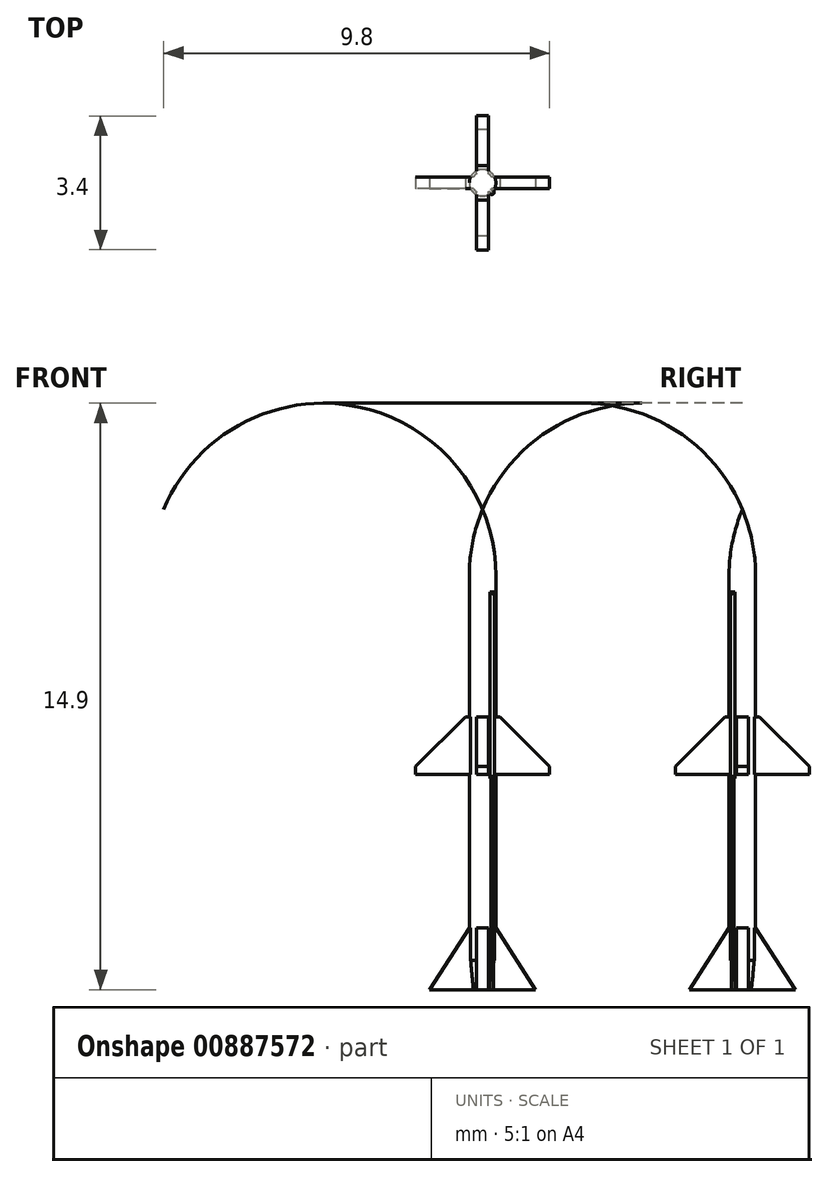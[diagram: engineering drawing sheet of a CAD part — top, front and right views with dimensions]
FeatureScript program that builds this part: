
annotation { "Feature Type Name" : "Feature", "Feature Type Description" : "" }
export const myFeature = defineFeature(function(context is Context, id is Id, definition is map)
    precondition{}
    {
        {
            var Q0;
            Q0=qCreatedBy(makeId("Front.planeOp"),FACE);
            var sketch = newSketch(context, id + "F0", { "sketchPlane" : qUnion([Q0])});
            skLineSegment(sketch, "E0", {"start": v(0, 0) * mm, "end": v(0, 12.2) * mm});
            skLineSegment(sketch, "E1", {"start": v(0.34, 10.5) * mm, "end": v(0.34, 0) * mm});
            skLineSegment(sketch, "E2", {"start": v(0.34, 0) * mm, "end": v(0, 0) * mm});
            skArc(sketch, "E3", {"start": v(0.34, 10.5) * mm, "mid": v(0.25, 11.37) * mm, "end": v(0, 12.2) * mm});
            skSolve(sketch);
        }
        {
            var Q0;
            Q0=makeQuery(id+"F0.imprint","IMPRINT",FACE,{"disambiguationData":[TD([[makeQuery(id+"F0.imprint","IMPRINT",EDGE,{"derivedFrom":sQuery(id+"F0.wireOp",EDGE,"E0")}),-1.0]])]});
            var Q1;
            Q1=sQuery(id+"F0.wireOp",EDGE,"E0");
            revolve(context, id + "F1", {"surfaceOperationType" : NewSurfaceOperationType.NEW, "entities" : qUnion([Q0]), "axis" : qUnion([Q1]), "revolveType" : RevolveType.FULL});
        }
        {
            var Q0;
            Q0=qCreatedBy(makeId("Front.planeOp"),FACE);
            var sketch = newSketch(context, id + "F2", { "sketchPlane" : qUnion([Q0])});
            skLineSegment(sketch, "E4", {"start": v(0.28, 0) * mm, "end": v(0.34, 0.75) * mm});
            skLineSegment(sketch, "E5", {"start": v(0.34, 0.75) * mm, "end": v(1.27, 0.75) * mm});
            skLineSegment(sketch, "E6", {"start": v(1.27, 0.75) * mm, "end": v(1.27, 0) * mm});
            skLineSegment(sketch, "E7", {"start": v(1.27, 0) * mm, "end": v(0.28, 0) * mm});
            skLineSegment(sketch, "E8.0", {"start": v(0.34, 0) * mm, "end": v(-0.34, 0) * mm});
            skSolve(sketch);
        }
        {
            var Q0;
            Q0=qSketchRegion(id+"F2",true);
            var Q1;
            Q1=makeQuery(id+"F1.opRevolve","SWEPT_FACE",FACE,{"disambiguationData":[OSD([sQuery(id+"F0.wireOp",EDGE,"E1")])]});
            revolve(context, id + "F3", {"operationType" : NewBodyOperationType.REMOVE, "surfaceOperationType" : NewSurfaceOperationType.NEW, "entities" : qUnion([Q0]), "axis" : qUnion([Q1]), "revolveType" : RevolveType.FULL, "oppositeDirection" : true});
        }
        {
            var Q0;
            Q0=qCreatedBy(makeId("Front.planeOp"),FACE);
            var sketch = newSketch(context, id + "F4", { "sketchPlane" : qUnion([Q0])});
            skLineSegment(sketch, "E9", {"start": v(-0.34, 6.93) * mm, "end": v(0.34, 6.93) * mm});
            skLineSegment(sketch, "E10", {"start": v(1.7, 5.47) * mm, "end": v(0.34, 5.47) * mm});
            skLineSegment(sketch, "E11", {"start": v(0.34, 1.57) * mm, "end": v(1.35, 0) * mm});
            skLineSegment(sketch, "E12", {"start": v(1.35, 0) * mm, "end": v(-1.35, 0) * mm});
            skLineSegment(sketch, "E13", {"start": v(-1.35, 0) * mm, "end": v(-0.34, 1.57) * mm});
            skLineSegment(sketch, "E14", {"start": v(-0.34, 5.47) * mm, "end": v(-1.7, 5.47) * mm});
            skLineSegment(sketch, "E15.0", {"start": v(0.34, 10.5) * mm, "end": v(-0.34, 10.5) * mm});
            skLineSegment(sketch, "E16.bottom", {"start": v(-0.06, 3) * mm, "end": v(0.06, 3) * mm});
            skLineSegment(sketch, "E16.top", {"start": v(-0.06, 0) * mm, "end": v(0.06, 0) * mm});
            skLineSegment(sketch, "E16.left", {"start": v(-0.06, 3) * mm, "end": v(-0.06, 0) * mm});
            skLineSegment(sketch, "E16.right", {"start": v(0.06, 3) * mm, "end": v(0.06, 0) * mm});
            skLineSegment(sketch, "E17", {"start": v(-1.7, 5.67) * mm, "end": v(-1.7, 5.47) * mm});
            skLineSegment(sketch, "E18", {"start": v(1.7, 5.47) * mm, "end": v(1.7, 5.67) * mm});
            skLineSegment(sketch, "E19", {"start": v(-0.34, 6.93) * mm, "end": v(-0.44, 6.93) * mm});
            skLineSegment(sketch, "E20", {"start": v(-0.44, 6.93) * mm, "end": v(-1.7, 5.67) * mm});
            skLineSegment(sketch, "E21", {"start": v(0.34, 6.93) * mm, "end": v(0.44, 6.93) * mm});
            skLineSegment(sketch, "E22", {"start": v(0.44, 6.93) * mm, "end": v(1.7, 5.67) * mm});
            skLineSegment(sketch, "E23.0", {"start": v(0.34, 0.75) * mm, "end": v(-0.34, 0.75) * mm});
            skLineSegment(sketch, "E24", {"start": v(-0.34, 5.47) * mm, "end": v(0.34, 5.47) * mm});
            skLineSegment(sketch, "E25", {"start": v(-0.34, 1.57) * mm, "end": v(0.34, 1.57) * mm});
            skSolve(sketch);
        }
        {
            var Q0;
            Q0=makeQuery(id+"F4.imprint","IMPRINT",FACE,{"disambiguationData":[TD([[makeQuery(id+"F4.imprint","IMPRINT",EDGE,{"derivedFrom":sQuery(id+"F4.wireOp",EDGE,"E9")}),-1.0]])]});
            var Q1;
            {var subQ6=sQuery(id+"F4.wireOp",EDGE,"E13");Q1=makeQuery(id+"F4.imprint","IMPRINT",FACE,{"disambiguationData":[TD([[makeQuery(id+"F4.imprint","IMPRINT",EDGE,{"derivedFrom":subQ6}),-1.0]])]});}
            var Q2;
            {var subQ4=sQuery(id+"F4.wireOp",EDGE,"E11");Q2=makeQuery(id+"F4.imprint","IMPRINT",FACE,{"disambiguationData":[TD([[makeQuery(id+"F4.imprint","IMPRINT",EDGE,{"derivedFrom":subQ4}),-1.0]])]});}
            extrude(context, id + "F5", {"entities" : qUnion([Q0, Q1, Q2]), "operationType" : NewBodyOperationType.ADD, "oppositeDirection" : true, "depth" : .3 * mm, "offsetDistance" : 25 * mm, "symmetric" : true});
        }
        {
            var Q0;
            Q0=makeQuery(id+"F1.opRevolve","SWEPT_BODY",BODY,{"disambiguationData":[OSD([sQuery(id+"F0.wireOp",EDGE,"E0"),sQuery(id+"F0.wireOp",EDGE,"E1"),sQuery(id+"F0.wireOp",EDGE,"E2"),sQuery(id+"F0.wireOp",EDGE,"E3")])]});
            var Q1;
            Q1=makeQuery(id+"F1.opRevolve","SWEPT_FACE",FACE,{"disambiguationData":[OSD([sQuery(id+"F0.wireOp",EDGE,"E1")])]});
            circularPattern(context, id + "F6", {"operationType" : NewBodyOperationType.ADD, "entities" : qUnion([Q0]), "axis" : qUnion([Q1]), "angle" : 360 * degree, "instanceCount" : 4, "equalSpace" : true, "computeTransformsWithoutBuiltin" : true});
        }
        {
            var Q0;
            {var subQ0=sQuery(id+"F4.wireOp",EDGE,"E24");var subQ5=sQuery(id+"F4.wireOp",EDGE,"E18");var subQ7=sQuery(id+"F4.wireOp",EDGE,"E14");var subQ8=sQuery(id+"F4.wireOp",EDGE,"E10");Q0=makeQuery(id+"F6.opPattern","COPY",FACE,{"derivedFrom":makeQuery(id+"F5.boolean.opBoolean","SPLIT",FACE,{"disambiguationData":[TD([makeQuery(id+"F5.opExtrude","SWEPT_FACE",FACE,{"disambiguationData":[OSD([subQ5])]})])],"derivedFrom":makeQuery(id+"F5.opExtrude","SWEPT_FACE",FACE,{"disambiguationData":[OSD([subQ8,subQ7,subQ0])]})}),"instanceName":"1"});}
            var sketch = newSketch(context, id + "F7", { "sketchPlane" : qUnion([Q0])});
            skLineSegment(sketch, "E26", {"start": v(0.05, 0.14) * mm, "end": v(0.14, 0.05) * mm});
            skLineSegment(sketch, "E27", {"start": v(0.14, 0.05) * mm, "end": v(0.28, 0.2) * mm});
            skLineSegment(sketch, "E28", {"start": v(0.05, 0.14) * mm, "end": v(0.2, 0.28) * mm});
            skLineSegment(sketch, "E29", {"start": v(0, 0) * mm, "end": v(0.1, 0.1) * mm, "construction": true});
            skArc(sketch, "E30", {"start": v(0.28, 0.2) * mm, "mid": v(0.28, 0.28) * mm, "end": v(0.2, 0.28) * mm});
            skLineSegment(sketch, "E31", {"start": v(0, 0) * mm, "end": v(0.1, 0) * mm, "construction": true});
            skSolve(sketch);
        }
        {
            var Q0;
            Q0=qSketchRegion(id+"F7",true);
            extrude(context, id + "F8", {"entities" : qUnion([Q0]), "operationType" : NewBodyOperationType.ADD, "oppositeDirection" : true, "depth" : (1360 / 300) * mm, "offsetDistance" : 25 * mm});
        }
        {
            var Q0;
            Q0=makeQuery(id+"F1.opRevolve","SWEPT_FACE",FACE,{"disambiguationData":[OSD([sQuery(id+"F0.wireOp",EDGE,"E2")])]});
            var sketch = newSketch(context, id + "F9", { "sketchPlane" : qUnion([Q0])});
            skLineSegment(sketch, "E32", {"start": v(0, 0) * mm, "end": v(0, 0) * mm});
            skLineSegment(sketch, "E33", {"start": v(0, 0) * mm, "end": v(0.44, 0) * mm, "construction": true});
            skCircle(sketch, "E34.0.0", {"center": v(0, 0) * mm, "radius": 0.28 * mm});
            skLineSegment(sketch, "E35", {"start": v(0.21, 0.26) * mm, "end": v(0.17, 0.22) * mm});
            skLineSegment(sketch, "E36", {"start": v(0.17, 0.22) * mm, "end": v(0.22, 0.17) * mm});
            skLineSegment(sketch, "E37", {"start": v(0.22, 0.17) * mm, "end": v(0.26, 0.21) * mm});
            skLineSegment(sketch, "E38", {"start": v(0, 0) * mm, "end": v(0.2, 0.2) * mm, "construction": true});
            skCircle(sketch, "E39.0", {"center": v(0, 0) * mm, "radius": 0.34 * mm});
            skArc(sketch, "E40", {"start": v(0.26, 0.21) * mm, "mid": v(0.26, 0.26) * mm, "end": v(0.21, 0.26) * mm});
            skLineSegment(sketch, "E41", {"start": v(0.21, 0.26) * mm, "end": v(0.26, 0.21) * mm, "construction": true});
            skSolve(sketch);
        }
        {
            var Q0;
            {var subQ0=sQuery(id+"F9.wireOp",EDGE,"E40");Q0=makeQuery(id+"F9.imprint","IMPRINT",FACE,{"disambiguationData":[TD([[makeQuery(id+"F9.imprint","IMPRINT",EDGE,{"derivedFrom":subQ0}),1.0]])]});}
            var Q1;
            {var subQ1=sQuery(id+"F9.wireOp",EDGE,"E35");Q1=makeQuery(id+"F9.imprint","IMPRINT",FACE,{"disambiguationData":[TD([[makeQuery(id+"F9.imprint","IMPRINT",EDGE,{"derivedFrom":subQ1}),1.0]])]});}
            extrude(context, id + "F10", {"entities" : qUnion([Q0, Q1]), "operationType" : NewBodyOperationType.ADD, "oppositeDirection" : true, "depth" : (1650 / 300) * mm, "offsetDistance" : 25 * mm});
        }
        {
            var Q0;
            Q0=makeQuery(id+"F8.boolean.opBoolean","INTERSECT",EDGE,{"derivedFrom":[makeQuery(id+"F1SgjpEdBBOFuZJ_3.boolean.opBoolean","SPLIT",FACE,{"disambiguationData":[TD([makeQuery(id+"F1.opRevolve","SWEPT_FACE",FACE,{"disambiguationData":[OSD([sQuery(id+"F0.wireOp",EDGE,"E3")])]})])],"derivedFrom":makeQuery(id+"F1.opRevolve","SWEPT_FACE",FACE,{"disambiguationData":[OSD([sQuery(id+"F0.wireOp",EDGE,"E1")])]})}),makeQuery(id+"F8.opExtrude","CAP_FACE",FACE,{"disambiguationData":[OSD([sQuery(id+"F7.wireOp",EDGE,"E26"),sQuery(id+"F7.wireOp",EDGE,"E27"),sQuery(id+"F7.wireOp",EDGE,"E28"),sQuery(id+"F7.wireOp",EDGE,"E30")])],"isStart":false})]});
            var Q1;
            Q1=makeQuery(id+"F10.boolean.opBoolean","SPLIT",EDGE,{"disambiguationData":[OD(0.0)],"derivedFrom":makeQuery(id+"F8.boolean.opBoolean","INTERSECT",EDGE,{"derivedFrom":[makeQuery(id+"F1.opRevolve","SWEPT_FACE",FACE,{"disambiguationData":[OSD([sQuery(id+"F0.wireOp",EDGE,"E1")])]}),makeQuery(id+"F8.opExtrude","CAP_FACE",FACE,{"disambiguationData":[OSD([sQuery(id+"F7.wireOp",EDGE,"E26"),sQuery(id+"F7.wireOp",EDGE,"E27"),sQuery(id+"F7.wireOp",EDGE,"E28"),sQuery(id+"F7.wireOp",EDGE,"E30")])],"isStart":true})]})});
            chamfer(context, id + "F11", {"entities" : qUnion([Q0, Q1]), "width" : .1 * mm, "tangentPropagation" : true});
        }
    });
